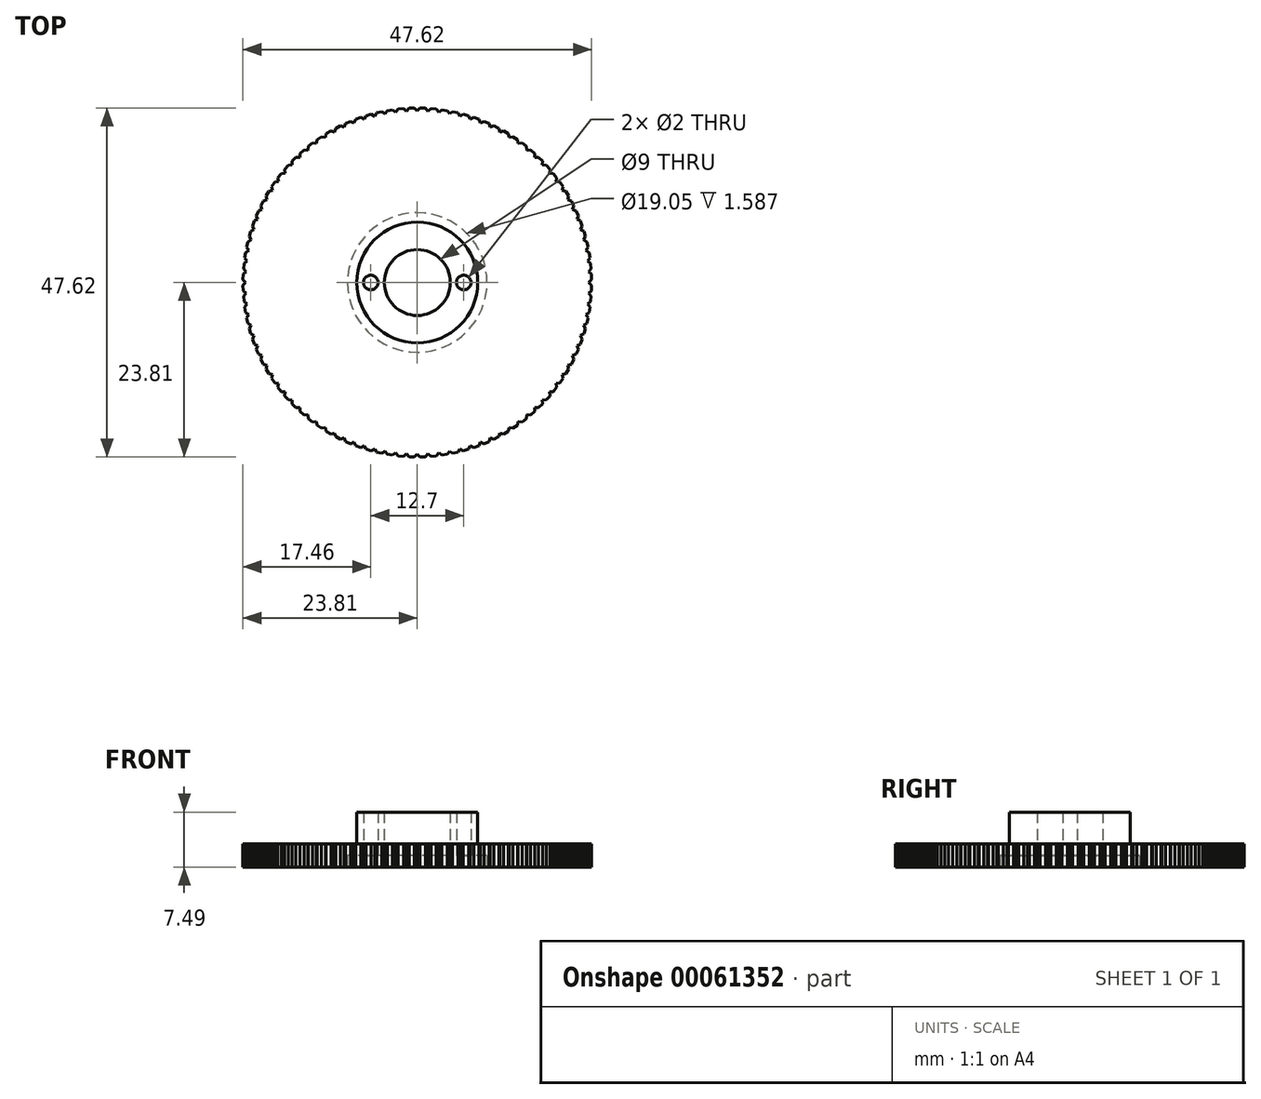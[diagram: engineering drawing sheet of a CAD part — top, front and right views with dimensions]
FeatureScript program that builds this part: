
annotation { "Feature Type Name" : "Feature", "Feature Type Description" : "" }
export const myFeature = defineFeature(function(context is Context, id is Id, definition is map)
    precondition{}
    {
        {
            var Q0;
            Q0=qCreatedBy(makeId("Top.planeOp"),FACE);
            var sketch = newSketch(context, id + "F0", { "sketchPlane" : qUnion([Q0])});
            skCircle(sketch, "E0", {"center": v(0, 0) * mm, "radius": 23.81 * mm});
            skCircle(sketch, "E1", {"center": v(0, 0) * mm, "radius": 8.26 * mm});
            skCircle(sketch, "E2", {"center": v(0, 0) * mm, "radius": 4.5 * mm});
            skSolve(sketch);
        }
        {
            var Q0;
            Q0=makeQuery(id+"F0.imprint","IMPRINT",FACE,{"disambiguationData":[TD([[makeQuery(id+"F0.imprint","IMPRINT",EDGE,{"derivedFrom":sQuery(id+"F0.wireOp",EDGE,"E0")}),1.0]])]});
            extrude(context, id + "F1", {"entities" : qUnion([Q0]), "depth" : 3.17 * mm});
        }
        {
            var Q0;
            Q0=makeQuery(id+"F0.imprint","IMPRINT",FACE,{"disambiguationData":[TD([[makeQuery(id+"F0.imprint","IMPRINT",EDGE,{"derivedFrom":sQuery(id+"F0.wireOp",EDGE,"E1")}),1.0]])]});
            extrude(context, id + "F2", {"entities" : qUnion([Q0]), "operationType" : NewBodyOperationType.ADD, "depth" : 7.5 * mm});
        }
        {
            var Q0;
            Q0=makeQuery(id+"F0.imprint","IMPRINT",FACE,{"disambiguationData":[TD([[makeQuery(id+"F0.imprint","IMPRINT",EDGE,{"derivedFrom":sQuery(id+"F0.wireOp",EDGE,"E0")}),1.0]])]});
            var sketch = newSketch(context, id + "F3", { "sketchPlane" : qUnion([Q0])});
            skCircle(sketch, "E3", {"center": v(0, 0) * mm, "radius": 9.53 * mm});
            skSolve(sketch);
        }
        {
            var Q0;
            Q0=makeQuery(id+"F3.imprint","IMPRINT",FACE,{"disambiguationData":[TD([[makeQuery(id+"F3.imprint","IMPRINT",EDGE,{"derivedFrom":sQuery(id+"F3.wireOp",EDGE,"E3")}),1.0]])]});
            var Q1;
            Q1=makeQuery(id+"F3.imprint","IMPRINT",FACE,{"disambiguationData":[TD([[makeQuery(id+"F3.imprint","IMPRINT",EDGE,{"derivedFrom":makeQuery(id+"F0.imprint","IMPRINT",EDGE,{"derivedFrom":sQuery(id+"F0.wireOp",EDGE,"E1")})}),1.0]])]});
            extrude(context, id + "F4", {"entities" : qUnion([Q0, Q1]), "operationType" : NewBodyOperationType.REMOVE, "depth" : 1.59 * mm});
        }
        {
            var Q0;
            Q0=makeQuery(id+"F4.boolean.opBoolean","COPY",FACE,{"derivedFrom":makeQuery(id+"F4.opExtrude","CAP_FACE",FACE,{"disambiguationData":[OSD([sQuery(id+"F3.wireOp",EDGE,"E3")])],"isStart":false})});
            var sketch = newSketch(context, id + "F5", { "sketchPlane" : qUnion([Q0])});
            skCircle(sketch, "E4", {"center": v(0, 0) * mm, "radius": 6.35 * mm});
            skPoint(sketch, "E5", {"position": v(-6.35, 0) * mm});
            skPoint(sketch, "E6", {"position": v(6.35, 0) * mm});
            skSolve(sketch);
        }
        {
            var Q0;
            Q0=sQuery(id+"F5.wireOp",VERTEX,"E5");
            var Q1;
            Q1=sQuery(id+"F5.wireOp",VERTEX,"E6");
            var Q2;
            Q2=makeQuery(id+"F1.opExtrude","SWEPT_BODY",BODY,{"disambiguationData":[OSD([sQuery(id+"F0.wireOp",EDGE,"E0"),sQuery(id+"F0.wireOp",EDGE,"E1")])]});
            hole(context, id + "F6", {"style" : HoleStyle.SIMPLE, "holeDiameter" : 2 * mm, "endStyle" : HoleEndStyle.THROUGH, "locations" : qUnion([Q0, Q1]), "scope" : qUnion([Q2])});
        }
        {
            var Q0;
            Q0=makeQuery(id+"F1.opExtrude","CAP_FACE",FACE,{"disambiguationData":[OSD([sQuery(id+"F0.wireOp",EDGE,"E0"),sQuery(id+"F0.wireOp",EDGE,"E1")])],"isStart":false});
            var sketch = newSketch(context, id + "F7", { "sketchPlane" : qUnion([Q0])});
            skLineSegment(sketch, "E7", {"start": v(0.37, 23.8) * mm, "end": v(0, 23.44) * mm});
            skLineSegment(sketch, "E8", {"start": v(0, 23.44) * mm, "end": v(-0.37, 23.8) * mm});
            skLineSegment(sketch, "E9.1.0", {"start": v(-1.47, 23.4) * mm, "end": v(-1.87, 23.74) * mm});
            skLineSegment(sketch, "E9.1.1", {"start": v(-1.12, 23.79) * mm, "end": v(-1.47, 23.4) * mm});
            skLineSegment(sketch, "E9.2.0", {"start": v(-2.94, 23.25) * mm, "end": v(-3.36, 23.57) * mm});
            skLineSegment(sketch, "E9.2.1", {"start": v(-2.61, 23.67) * mm, "end": v(-2.94, 23.25) * mm});
            skPoint(sketch, "E9.center", {"position": v(0, 0) * mm});
            skLineSegment(sketch, "E10.1.3.0", {"start": v(-4.4, 23.02) * mm, "end": v(-4.83, 23.32) * mm});
            skLineSegment(sketch, "E10.3.3.0", {"start": v(-4.1, 23.46) * mm, "end": v(-4.4, 23.02) * mm});
            skLineSegment(sketch, "E10.1.4.0", {"start": v(-5.83, 22.7) * mm, "end": v(-6.28, 22.97) * mm});
            skLineSegment(sketch, "E10.3.4.0", {"start": v(-5.56, 23.15) * mm, "end": v(-5.83, 22.7) * mm});
            skLineSegment(sketch, "E10.1.5.0", {"start": v(-7.24, 22.3) * mm, "end": v(-7.71, 22.53) * mm});
            skLineSegment(sketch, "E10.3.5.0", {"start": v(-7, 22.76) * mm, "end": v(-7.24, 22.3) * mm});
            skLineSegment(sketch, "E10.1.6.0", {"start": v(-8.63, 21.8) * mm, "end": v(-9.11, 22) * mm});
            skLineSegment(sketch, "E10.3.6.0", {"start": v(-8.42, 22.28) * mm, "end": v(-8.63, 21.8) * mm});
            skLineSegment(sketch, "E10.1.7.0", {"start": v(-9.98, 21.2) * mm, "end": v(-10.48, 21.38) * mm});
            skLineSegment(sketch, "E10.3.7.0", {"start": v(-9.8, 21.7) * mm, "end": v(-9.98, 21.2) * mm});
            skLineSegment(sketch, "E10.1.8.0", {"start": v(-11.3, 20.54) * mm, "end": v(-11.8, 20.68) * mm});
            skLineSegment(sketch, "E10.3.8.0", {"start": v(-11.14, 21.04) * mm, "end": v(-11.3, 20.54) * mm});
            skLineSegment(sketch, "E10.1.9.0", {"start": v(-12.56, 19.79) * mm, "end": v(-13.07, 19.9) * mm});
            skLineSegment(sketch, "E10.3.9.0", {"start": v(-12.44, 20.3) * mm, "end": v(-12.56, 19.79) * mm});
            skLineSegment(sketch, "E10.1.10.0", {"start": v(-13.78, 18.96) * mm, "end": v(-14.3, 19.04) * mm});
            skLineSegment(sketch, "E10.3.10.0", {"start": v(-13.7, 19.48) * mm, "end": v(-13.78, 18.96) * mm});
            skLineSegment(sketch, "E10.1.11.0", {"start": v(-14.94, 18.06) * mm, "end": v(-15.46, 18.1) * mm});
            skLineSegment(sketch, "E10.3.11.0", {"start": v(-14.89, 18.58) * mm, "end": v(-14.94, 18.06) * mm});
            skLineSegment(sketch, "E10.1.12.0", {"start": v(-16.04, 17.09) * mm, "end": v(-16.57, 17.1) * mm});
            skLineSegment(sketch, "E10.3.12.0", {"start": v(-16.03, 17.61) * mm, "end": v(-16.04, 17.09) * mm});
            skLineSegment(sketch, "E10.1.13.0", {"start": v(-17.09, 16.04) * mm, "end": v(-17.61, 16.03) * mm});
            skLineSegment(sketch, "E10.3.13.0", {"start": v(-17.1, 16.57) * mm, "end": v(-17.09, 16.04) * mm});
            skLineSegment(sketch, "E10.1.14.0", {"start": v(-18.06, 14.94) * mm, "end": v(-18.58, 14.89) * mm});
            skLineSegment(sketch, "E10.3.14.0", {"start": v(-18.1, 15.46) * mm, "end": v(-18.06, 14.94) * mm});
            skLineSegment(sketch, "E10.1.15.0", {"start": v(-18.96, 13.78) * mm, "end": v(-19.48, 13.7) * mm});
            skLineSegment(sketch, "E10.3.15.0", {"start": v(-19.04, 14.3) * mm, "end": v(-18.96, 13.78) * mm});
            skLineSegment(sketch, "E10.1.16.0", {"start": v(-19.79, 12.56) * mm, "end": v(-20.3, 12.44) * mm});
            skLineSegment(sketch, "E10.3.16.0", {"start": v(-19.9, 13.07) * mm, "end": v(-19.79, 12.56) * mm});
            skLineSegment(sketch, "E10.1.17.0", {"start": v(-20.54, 11.3) * mm, "end": v(-21.04, 11.14) * mm});
            skLineSegment(sketch, "E10.3.17.0", {"start": v(-20.68, 11.8) * mm, "end": v(-20.54, 11.3) * mm});
            skLineSegment(sketch, "E10.1.18.0", {"start": v(-21.2, 9.98) * mm, "end": v(-21.7, 9.8) * mm});
            skLineSegment(sketch, "E10.3.18.0", {"start": v(-21.38, 10.48) * mm, "end": v(-21.2, 9.98) * mm});
            skLineSegment(sketch, "E10.1.19.0", {"start": v(-21.8, 8.63) * mm, "end": v(-22.28, 8.42) * mm});
            skLineSegment(sketch, "E10.3.19.0", {"start": v(-22, 9.11) * mm, "end": v(-21.8, 8.63) * mm});
            skLineSegment(sketch, "E10.1.20.0", {"start": v(-22.3, 7.24) * mm, "end": v(-22.76, 7) * mm});
            skLineSegment(sketch, "E10.3.20.0", {"start": v(-22.53, 7.71) * mm, "end": v(-22.3, 7.24) * mm});
            skLineSegment(sketch, "E10.1.21.0", {"start": v(-22.7, 5.83) * mm, "end": v(-23.15, 5.56) * mm});
            skLineSegment(sketch, "E10.3.21.0", {"start": v(-22.97, 6.28) * mm, "end": v(-22.7, 5.83) * mm});
            skLineSegment(sketch, "E10.1.22.0", {"start": v(-23.02, 4.4) * mm, "end": v(-23.46, 4.1) * mm});
            skLineSegment(sketch, "E10.3.22.0", {"start": v(-23.32, 4.83) * mm, "end": v(-23.02, 4.4) * mm});
            skLineSegment(sketch, "E10.1.23.0", {"start": v(-23.25, 2.94) * mm, "end": v(-23.67, 2.61) * mm});
            skLineSegment(sketch, "E10.3.23.0", {"start": v(-23.57, 3.36) * mm, "end": v(-23.25, 2.94) * mm});
            skLineSegment(sketch, "E10.1.24.0", {"start": v(-23.4, 1.47) * mm, "end": v(-23.79, 1.12) * mm});
            skLineSegment(sketch, "E10.3.24.0", {"start": v(-23.74, 1.87) * mm, "end": v(-23.4, 1.47) * mm});
            skLineSegment(sketch, "E10.1.25.0", {"start": v(-23.44, 0) * mm, "end": v(-23.8, -0.37) * mm});
            skLineSegment(sketch, "E10.3.25.0", {"start": v(-23.8, 0.37) * mm, "end": v(-23.44, 0) * mm});
            skLineSegment(sketch, "E10.1.26.0", {"start": v(-23.4, -1.47) * mm, "end": v(-23.74, -1.87) * mm});
            skLineSegment(sketch, "E10.3.26.0", {"start": v(-23.79, -1.12) * mm, "end": v(-23.4, -1.47) * mm});
            skLineSegment(sketch, "E10.1.27.0", {"start": v(-23.25, -2.94) * mm, "end": v(-23.57, -3.36) * mm});
            skLineSegment(sketch, "E10.3.27.0", {"start": v(-23.67, -2.61) * mm, "end": v(-23.25, -2.94) * mm});
            skLineSegment(sketch, "E10.1.28.0", {"start": v(-23.02, -4.4) * mm, "end": v(-23.32, -4.83) * mm});
            skLineSegment(sketch, "E10.3.28.0", {"start": v(-23.46, -4.1) * mm, "end": v(-23.02, -4.4) * mm});
            skLineSegment(sketch, "E10.1.29.0", {"start": v(-22.7, -5.83) * mm, "end": v(-22.97, -6.28) * mm});
            skLineSegment(sketch, "E10.3.29.0", {"start": v(-23.15, -5.56) * mm, "end": v(-22.7, -5.83) * mm});
            skLineSegment(sketch, "E10.1.30.0", {"start": v(-22.3, -7.24) * mm, "end": v(-22.53, -7.71) * mm});
            skLineSegment(sketch, "E10.3.30.0", {"start": v(-22.76, -7) * mm, "end": v(-22.3, -7.24) * mm});
            skLineSegment(sketch, "E10.1.31.0", {"start": v(-21.8, -8.63) * mm, "end": v(-22, -9.11) * mm});
            skLineSegment(sketch, "E10.3.31.0", {"start": v(-22.28, -8.42) * mm, "end": v(-21.8, -8.63) * mm});
            skLineSegment(sketch, "E10.1.32.0", {"start": v(-21.2, -9.98) * mm, "end": v(-21.38, -10.48) * mm});
            skLineSegment(sketch, "E10.3.32.0", {"start": v(-21.7, -9.8) * mm, "end": v(-21.2, -9.98) * mm});
            skLineSegment(sketch, "E10.1.33.0", {"start": v(-20.54, -11.3) * mm, "end": v(-20.68, -11.8) * mm});
            skLineSegment(sketch, "E10.3.33.0", {"start": v(-21.04, -11.14) * mm, "end": v(-20.54, -11.3) * mm});
            skLineSegment(sketch, "E10.1.34.0", {"start": v(-19.79, -12.56) * mm, "end": v(-19.9, -13.07) * mm});
            skLineSegment(sketch, "E10.3.34.0", {"start": v(-20.3, -12.44) * mm, "end": v(-19.79, -12.56) * mm});
            skLineSegment(sketch, "E10.1.35.0", {"start": v(-18.96, -13.78) * mm, "end": v(-19.04, -14.3) * mm});
            skLineSegment(sketch, "E10.3.35.0", {"start": v(-19.48, -13.7) * mm, "end": v(-18.96, -13.78) * mm});
            skLineSegment(sketch, "E10.1.36.0", {"start": v(-18.06, -14.94) * mm, "end": v(-18.1, -15.46) * mm});
            skLineSegment(sketch, "E10.3.36.0", {"start": v(-18.58, -14.89) * mm, "end": v(-18.06, -14.94) * mm});
            skLineSegment(sketch, "E10.1.37.0", {"start": v(-17.09, -16.04) * mm, "end": v(-17.1, -16.57) * mm});
            skLineSegment(sketch, "E10.3.37.0", {"start": v(-17.61, -16.03) * mm, "end": v(-17.09, -16.04) * mm});
            skLineSegment(sketch, "E10.1.38.0", {"start": v(-16.04, -17.09) * mm, "end": v(-16.03, -17.61) * mm});
            skLineSegment(sketch, "E10.3.38.0", {"start": v(-16.57, -17.1) * mm, "end": v(-16.04, -17.09) * mm});
            skLineSegment(sketch, "E10.1.39.0", {"start": v(-14.94, -18.06) * mm, "end": v(-14.89, -18.58) * mm});
            skLineSegment(sketch, "E10.3.39.0", {"start": v(-15.46, -18.1) * mm, "end": v(-14.94, -18.06) * mm});
            skLineSegment(sketch, "E10.1.40.0", {"start": v(-13.78, -18.96) * mm, "end": v(-13.7, -19.48) * mm});
            skLineSegment(sketch, "E10.3.40.0", {"start": v(-14.3, -19.04) * mm, "end": v(-13.78, -18.96) * mm});
            skLineSegment(sketch, "E10.1.41.0", {"start": v(-12.56, -19.79) * mm, "end": v(-12.44, -20.3) * mm});
            skLineSegment(sketch, "E10.3.41.0", {"start": v(-13.07, -19.9) * mm, "end": v(-12.56, -19.79) * mm});
            skLineSegment(sketch, "E10.1.42.0", {"start": v(-11.3, -20.54) * mm, "end": v(-11.14, -21.04) * mm});
            skLineSegment(sketch, "E10.3.42.0", {"start": v(-11.8, -20.68) * mm, "end": v(-11.3, -20.54) * mm});
            skLineSegment(sketch, "E10.1.43.0", {"start": v(-9.98, -21.2) * mm, "end": v(-9.8, -21.7) * mm});
            skLineSegment(sketch, "E10.3.43.0", {"start": v(-10.48, -21.38) * mm, "end": v(-9.98, -21.2) * mm});
            skLineSegment(sketch, "E10.1.44.0", {"start": v(-8.63, -21.8) * mm, "end": v(-8.42, -22.28) * mm});
            skLineSegment(sketch, "E10.3.44.0", {"start": v(-9.11, -22) * mm, "end": v(-8.63, -21.8) * mm});
            skLineSegment(sketch, "E10.1.45.0", {"start": v(-7.24, -22.3) * mm, "end": v(-7, -22.76) * mm});
            skLineSegment(sketch, "E10.3.45.0", {"start": v(-7.71, -22.53) * mm, "end": v(-7.24, -22.3) * mm});
            skLineSegment(sketch, "E10.1.46.0", {"start": v(-5.83, -22.7) * mm, "end": v(-5.56, -23.15) * mm});
            skLineSegment(sketch, "E10.3.46.0", {"start": v(-6.28, -22.97) * mm, "end": v(-5.83, -22.7) * mm});
            skLineSegment(sketch, "E10.1.47.0", {"start": v(-4.4, -23.02) * mm, "end": v(-4.1, -23.46) * mm});
            skLineSegment(sketch, "E10.3.47.0", {"start": v(-4.83, -23.32) * mm, "end": v(-4.4, -23.02) * mm});
            skLineSegment(sketch, "E10.1.48.0", {"start": v(-2.94, -23.25) * mm, "end": v(-2.61, -23.67) * mm});
            skLineSegment(sketch, "E10.3.48.0", {"start": v(-3.36, -23.57) * mm, "end": v(-2.94, -23.25) * mm});
            skLineSegment(sketch, "E10.1.49.0", {"start": v(-1.47, -23.4) * mm, "end": v(-1.12, -23.79) * mm});
            skLineSegment(sketch, "E10.3.49.0", {"start": v(-1.87, -23.74) * mm, "end": v(-1.47, -23.4) * mm});
            skLineSegment(sketch, "E10.1.50.0", {"start": v(0, -23.44) * mm, "end": v(0.37, -23.8) * mm});
            skLineSegment(sketch, "E10.3.50.0", {"start": v(-0.37, -23.8) * mm, "end": v(0, -23.44) * mm});
            skLineSegment(sketch, "E10.1.51.0", {"start": v(1.47, -23.4) * mm, "end": v(1.87, -23.74) * mm});
            skLineSegment(sketch, "E10.3.51.0", {"start": v(1.12, -23.79) * mm, "end": v(1.47, -23.4) * mm});
            skLineSegment(sketch, "E10.1.52.0", {"start": v(2.94, -23.25) * mm, "end": v(3.36, -23.57) * mm});
            skLineSegment(sketch, "E10.3.52.0", {"start": v(2.61, -23.67) * mm, "end": v(2.94, -23.25) * mm});
            skLineSegment(sketch, "E10.1.53.0", {"start": v(4.4, -23.02) * mm, "end": v(4.83, -23.32) * mm});
            skLineSegment(sketch, "E10.3.53.0", {"start": v(4.1, -23.46) * mm, "end": v(4.4, -23.02) * mm});
            skLineSegment(sketch, "E10.1.54.0", {"start": v(5.83, -22.7) * mm, "end": v(6.28, -22.97) * mm});
            skLineSegment(sketch, "E10.3.54.0", {"start": v(5.56, -23.15) * mm, "end": v(5.83, -22.7) * mm});
            skLineSegment(sketch, "E10.1.55.0", {"start": v(7.24, -22.3) * mm, "end": v(7.71, -22.53) * mm});
            skLineSegment(sketch, "E10.3.55.0", {"start": v(7, -22.76) * mm, "end": v(7.24, -22.3) * mm});
            skLineSegment(sketch, "E10.1.56.0", {"start": v(8.63, -21.8) * mm, "end": v(9.11, -22) * mm});
            skLineSegment(sketch, "E10.3.56.0", {"start": v(8.42, -22.28) * mm, "end": v(8.63, -21.8) * mm});
            skLineSegment(sketch, "E10.1.57.0", {"start": v(9.98, -21.2) * mm, "end": v(10.48, -21.38) * mm});
            skLineSegment(sketch, "E10.3.57.0", {"start": v(9.8, -21.7) * mm, "end": v(9.98, -21.2) * mm});
            skLineSegment(sketch, "E10.1.58.0", {"start": v(11.3, -20.54) * mm, "end": v(11.8, -20.68) * mm});
            skLineSegment(sketch, "E10.3.58.0", {"start": v(11.14, -21.04) * mm, "end": v(11.3, -20.54) * mm});
            skLineSegment(sketch, "E10.1.59.0", {"start": v(12.56, -19.79) * mm, "end": v(13.07, -19.9) * mm});
            skLineSegment(sketch, "E10.3.59.0", {"start": v(12.44, -20.3) * mm, "end": v(12.56, -19.79) * mm});
            skLineSegment(sketch, "E10.1.60.0", {"start": v(13.78, -18.96) * mm, "end": v(14.3, -19.04) * mm});
            skLineSegment(sketch, "E10.3.60.0", {"start": v(13.7, -19.48) * mm, "end": v(13.78, -18.96) * mm});
            skLineSegment(sketch, "E10.1.61.0", {"start": v(14.94, -18.06) * mm, "end": v(15.46, -18.1) * mm});
            skLineSegment(sketch, "E10.3.61.0", {"start": v(14.89, -18.58) * mm, "end": v(14.94, -18.06) * mm});
            skLineSegment(sketch, "E10.1.62.0", {"start": v(16.04, -17.09) * mm, "end": v(16.57, -17.1) * mm});
            skLineSegment(sketch, "E10.3.62.0", {"start": v(16.03, -17.61) * mm, "end": v(16.04, -17.09) * mm});
            skLineSegment(sketch, "E10.1.63.0", {"start": v(17.09, -16.04) * mm, "end": v(17.61, -16.03) * mm});
            skLineSegment(sketch, "E10.3.63.0", {"start": v(17.1, -16.57) * mm, "end": v(17.09, -16.04) * mm});
            skLineSegment(sketch, "E10.1.64.0", {"start": v(18.06, -14.94) * mm, "end": v(18.58, -14.89) * mm});
            skLineSegment(sketch, "E10.3.64.0", {"start": v(18.1, -15.46) * mm, "end": v(18.06, -14.94) * mm});
            skLineSegment(sketch, "E10.1.65.0", {"start": v(18.96, -13.78) * mm, "end": v(19.48, -13.7) * mm});
            skLineSegment(sketch, "E10.3.65.0", {"start": v(19.04, -14.3) * mm, "end": v(18.96, -13.78) * mm});
            skLineSegment(sketch, "E10.1.66.0", {"start": v(19.79, -12.56) * mm, "end": v(20.3, -12.44) * mm});
            skLineSegment(sketch, "E10.3.66.0", {"start": v(19.9, -13.07) * mm, "end": v(19.79, -12.56) * mm});
            skLineSegment(sketch, "E10.1.67.0", {"start": v(20.54, -11.3) * mm, "end": v(21.04, -11.14) * mm});
            skLineSegment(sketch, "E10.3.67.0", {"start": v(20.68, -11.8) * mm, "end": v(20.54, -11.3) * mm});
            skLineSegment(sketch, "E10.1.68.0", {"start": v(21.2, -9.98) * mm, "end": v(21.7, -9.8) * mm});
            skLineSegment(sketch, "E10.3.68.0", {"start": v(21.38, -10.48) * mm, "end": v(21.2, -9.98) * mm});
            skLineSegment(sketch, "E10.1.69.0", {"start": v(21.8, -8.63) * mm, "end": v(22.28, -8.42) * mm});
            skLineSegment(sketch, "E10.3.69.0", {"start": v(22, -9.11) * mm, "end": v(21.8, -8.63) * mm});
            skLineSegment(sketch, "E10.1.70.0", {"start": v(22.3, -7.24) * mm, "end": v(22.76, -7) * mm});
            skLineSegment(sketch, "E10.3.70.0", {"start": v(22.53, -7.71) * mm, "end": v(22.3, -7.24) * mm});
            skLineSegment(sketch, "E10.1.71.0", {"start": v(22.7, -5.83) * mm, "end": v(23.15, -5.56) * mm});
            skLineSegment(sketch, "E10.3.71.0", {"start": v(22.97, -6.28) * mm, "end": v(22.7, -5.83) * mm});
            skLineSegment(sketch, "E10.1.72.0", {"start": v(23.02, -4.4) * mm, "end": v(23.46, -4.1) * mm});
            skLineSegment(sketch, "E10.3.72.0", {"start": v(23.32, -4.83) * mm, "end": v(23.02, -4.4) * mm});
            skLineSegment(sketch, "E10.1.73.0", {"start": v(23.25, -2.94) * mm, "end": v(23.67, -2.61) * mm});
            skLineSegment(sketch, "E10.3.73.0", {"start": v(23.57, -3.36) * mm, "end": v(23.25, -2.94) * mm});
            skLineSegment(sketch, "E10.1.74.0", {"start": v(23.4, -1.47) * mm, "end": v(23.79, -1.12) * mm});
            skLineSegment(sketch, "E10.3.74.0", {"start": v(23.74, -1.87) * mm, "end": v(23.4, -1.47) * mm});
            skLineSegment(sketch, "E10.1.75.0", {"start": v(23.44, 0) * mm, "end": v(23.8, 0.37) * mm});
            skLineSegment(sketch, "E10.3.75.0", {"start": v(23.8, -0.37) * mm, "end": v(23.44, 0) * mm});
            skLineSegment(sketch, "E10.1.76.0", {"start": v(23.4, 1.47) * mm, "end": v(23.74, 1.87) * mm});
            skLineSegment(sketch, "E10.3.76.0", {"start": v(23.79, 1.12) * mm, "end": v(23.4, 1.47) * mm});
            skLineSegment(sketch, "E10.1.77.0", {"start": v(23.25, 2.94) * mm, "end": v(23.57, 3.36) * mm});
            skLineSegment(sketch, "E10.3.77.0", {"start": v(23.67, 2.61) * mm, "end": v(23.25, 2.94) * mm});
            skLineSegment(sketch, "E10.1.78.0", {"start": v(23.02, 4.4) * mm, "end": v(23.32, 4.83) * mm});
            skLineSegment(sketch, "E10.3.78.0", {"start": v(23.46, 4.1) * mm, "end": v(23.02, 4.4) * mm});
            skLineSegment(sketch, "E10.1.79.0", {"start": v(22.7, 5.83) * mm, "end": v(22.97, 6.28) * mm});
            skLineSegment(sketch, "E10.3.79.0", {"start": v(23.15, 5.56) * mm, "end": v(22.7, 5.83) * mm});
            skLineSegment(sketch, "E10.1.80.0", {"start": v(22.3, 7.24) * mm, "end": v(22.53, 7.71) * mm});
            skLineSegment(sketch, "E10.3.80.0", {"start": v(22.76, 7) * mm, "end": v(22.3, 7.24) * mm});
            skLineSegment(sketch, "E10.1.81.0", {"start": v(21.8, 8.63) * mm, "end": v(22, 9.11) * mm});
            skLineSegment(sketch, "E10.3.81.0", {"start": v(22.28, 8.42) * mm, "end": v(21.8, 8.63) * mm});
            skLineSegment(sketch, "E10.1.82.0", {"start": v(21.2, 9.98) * mm, "end": v(21.38, 10.48) * mm});
            skLineSegment(sketch, "E10.3.82.0", {"start": v(21.7, 9.8) * mm, "end": v(21.2, 9.98) * mm});
            skLineSegment(sketch, "E10.1.83.0", {"start": v(20.54, 11.3) * mm, "end": v(20.68, 11.8) * mm});
            skLineSegment(sketch, "E10.3.83.0", {"start": v(21.04, 11.14) * mm, "end": v(20.54, 11.3) * mm});
            skLineSegment(sketch, "E10.1.84.0", {"start": v(19.79, 12.56) * mm, "end": v(19.9, 13.07) * mm});
            skLineSegment(sketch, "E10.3.84.0", {"start": v(20.3, 12.44) * mm, "end": v(19.79, 12.56) * mm});
            skLineSegment(sketch, "E10.1.85.0", {"start": v(18.96, 13.78) * mm, "end": v(19.04, 14.3) * mm});
            skLineSegment(sketch, "E10.3.85.0", {"start": v(19.48, 13.7) * mm, "end": v(18.96, 13.78) * mm});
            skLineSegment(sketch, "E10.1.86.0", {"start": v(18.06, 14.94) * mm, "end": v(18.1, 15.46) * mm});
            skLineSegment(sketch, "E10.3.86.0", {"start": v(18.58, 14.89) * mm, "end": v(18.06, 14.94) * mm});
            skLineSegment(sketch, "E10.1.87.0", {"start": v(17.09, 16.04) * mm, "end": v(17.1, 16.57) * mm});
            skLineSegment(sketch, "E10.3.87.0", {"start": v(17.61, 16.03) * mm, "end": v(17.09, 16.04) * mm});
            skLineSegment(sketch, "E10.1.88.0", {"start": v(16.04, 17.09) * mm, "end": v(16.03, 17.61) * mm});
            skLineSegment(sketch, "E10.3.88.0", {"start": v(16.57, 17.1) * mm, "end": v(16.04, 17.09) * mm});
            skLineSegment(sketch, "E10.1.89.0", {"start": v(14.94, 18.06) * mm, "end": v(14.89, 18.58) * mm});
            skLineSegment(sketch, "E10.3.89.0", {"start": v(15.46, 18.1) * mm, "end": v(14.94, 18.06) * mm});
            skLineSegment(sketch, "E10.1.90.0", {"start": v(13.78, 18.96) * mm, "end": v(13.7, 19.48) * mm});
            skLineSegment(sketch, "E10.3.90.0", {"start": v(14.3, 19.04) * mm, "end": v(13.78, 18.96) * mm});
            skLineSegment(sketch, "E10.1.91.0", {"start": v(12.56, 19.79) * mm, "end": v(12.44, 20.3) * mm});
            skLineSegment(sketch, "E10.3.91.0", {"start": v(13.07, 19.9) * mm, "end": v(12.56, 19.79) * mm});
            skLineSegment(sketch, "E10.1.92.0", {"start": v(11.3, 20.54) * mm, "end": v(11.14, 21.04) * mm});
            skLineSegment(sketch, "E10.3.92.0", {"start": v(11.8, 20.68) * mm, "end": v(11.3, 20.54) * mm});
            skLineSegment(sketch, "E10.1.93.0", {"start": v(9.98, 21.2) * mm, "end": v(9.8, 21.7) * mm});
            skLineSegment(sketch, "E10.3.93.0", {"start": v(10.48, 21.38) * mm, "end": v(9.98, 21.2) * mm});
            skLineSegment(sketch, "E10.1.94.0", {"start": v(8.63, 21.8) * mm, "end": v(8.42, 22.28) * mm});
            skLineSegment(sketch, "E10.3.94.0", {"start": v(9.11, 22) * mm, "end": v(8.63, 21.8) * mm});
            skLineSegment(sketch, "E10.1.95.0", {"start": v(7.24, 22.3) * mm, "end": v(7, 22.76) * mm});
            skLineSegment(sketch, "E10.3.95.0", {"start": v(7.71, 22.53) * mm, "end": v(7.24, 22.3) * mm});
            skLineSegment(sketch, "E10.1.96.0", {"start": v(5.83, 22.7) * mm, "end": v(5.56, 23.15) * mm});
            skLineSegment(sketch, "E10.3.96.0", {"start": v(6.28, 22.97) * mm, "end": v(5.83, 22.7) * mm});
            skLineSegment(sketch, "E10.1.97.0", {"start": v(4.4, 23.02) * mm, "end": v(4.1, 23.46) * mm});
            skLineSegment(sketch, "E10.3.97.0", {"start": v(4.83, 23.32) * mm, "end": v(4.4, 23.02) * mm});
            skLineSegment(sketch, "E10.1.98.0", {"start": v(2.94, 23.25) * mm, "end": v(2.61, 23.67) * mm});
            skLineSegment(sketch, "E10.3.98.0", {"start": v(3.36, 23.57) * mm, "end": v(2.94, 23.25) * mm});
            skLineSegment(sketch, "E10.1.99.0", {"start": v(1.47, 23.4) * mm, "end": v(1.12, 23.79) * mm});
            skLineSegment(sketch, "E10.3.99.0", {"start": v(1.87, 23.74) * mm, "end": v(1.47, 23.4) * mm});
            skLineSegment(sketch, "E11", {"start": v(-1.12, 23.79) * mm, "end": v(-0.37, 23.8) * mm});
            skLineSegment(sketch, "E12.1.0", {"start": v(-2.61, 23.67) * mm, "end": v(-1.87, 23.74) * mm});
            skLineSegment(sketch, "E12.2.0", {"start": v(-4.1, 23.46) * mm, "end": v(-3.36, 23.57) * mm});
            skLineSegment(sketch, "E12.3.0", {"start": v(-5.56, 23.15) * mm, "end": v(-4.83, 23.32) * mm});
            skLineSegment(sketch, "E12.4.0", {"start": v(-7, 22.76) * mm, "end": v(-6.28, 22.97) * mm});
            skLineSegment(sketch, "E12.5.0", {"start": v(-8.42, 22.28) * mm, "end": v(-7.71, 22.53) * mm});
            skLineSegment(sketch, "E12.6.0", {"start": v(-9.8, 21.7) * mm, "end": v(-9.11, 22) * mm});
            skLineSegment(sketch, "E12.7.0", {"start": v(-11.14, 21.04) * mm, "end": v(-10.48, 21.38) * mm});
            skLineSegment(sketch, "E12.8.0", {"start": v(-12.44, 20.3) * mm, "end": v(-11.8, 20.68) * mm});
            skLineSegment(sketch, "E12.9.0", {"start": v(-13.7, 19.48) * mm, "end": v(-13.07, 19.9) * mm});
            skLineSegment(sketch, "E12.10.0", {"start": v(-14.89, 18.58) * mm, "end": v(-14.3, 19.04) * mm});
            skLineSegment(sketch, "E12.11.0", {"start": v(-16.03, 17.61) * mm, "end": v(-15.46, 18.1) * mm});
            skLineSegment(sketch, "E12.12.0", {"start": v(-17.1, 16.57) * mm, "end": v(-16.57, 17.1) * mm});
            skLineSegment(sketch, "E12.13.0", {"start": v(-18.1, 15.46) * mm, "end": v(-17.61, 16.03) * mm});
            skLineSegment(sketch, "E12.14.0", {"start": v(-19.04, 14.3) * mm, "end": v(-18.58, 14.89) * mm});
            skLineSegment(sketch, "E12.15.0", {"start": v(-19.9, 13.07) * mm, "end": v(-19.48, 13.7) * mm});
            skLineSegment(sketch, "E12.16.0", {"start": v(-20.68, 11.8) * mm, "end": v(-20.3, 12.44) * mm});
            skLineSegment(sketch, "E12.17.0", {"start": v(-21.38, 10.48) * mm, "end": v(-21.04, 11.14) * mm});
            skLineSegment(sketch, "E12.18.0", {"start": v(-22, 9.11) * mm, "end": v(-21.7, 9.8) * mm});
            skLineSegment(sketch, "E12.19.0", {"start": v(-22.53, 7.71) * mm, "end": v(-22.28, 8.42) * mm});
            skLineSegment(sketch, "E12.20.0", {"start": v(-22.97, 6.28) * mm, "end": v(-22.76, 7) * mm});
            skLineSegment(sketch, "E12.21.0", {"start": v(-23.32, 4.83) * mm, "end": v(-23.15, 5.56) * mm});
            skLineSegment(sketch, "E12.22.0", {"start": v(-23.57, 3.36) * mm, "end": v(-23.46, 4.1) * mm});
            skLineSegment(sketch, "E12.23.0", {"start": v(-23.74, 1.87) * mm, "end": v(-23.67, 2.61) * mm});
            skLineSegment(sketch, "E12.24.0", {"start": v(-23.8, 0.37) * mm, "end": v(-23.79, 1.12) * mm});
            skLineSegment(sketch, "E12.25.0", {"start": v(-23.79, -1.12) * mm, "end": v(-23.8, -0.37) * mm});
            skLineSegment(sketch, "E12.26.0", {"start": v(-23.67, -2.61) * mm, "end": v(-23.74, -1.87) * mm});
            skLineSegment(sketch, "E12.27.0", {"start": v(-23.46, -4.1) * mm, "end": v(-23.57, -3.36) * mm});
            skLineSegment(sketch, "E12.28.0", {"start": v(-23.15, -5.56) * mm, "end": v(-23.32, -4.83) * mm});
            skLineSegment(sketch, "E12.29.0", {"start": v(-22.76, -7) * mm, "end": v(-22.97, -6.28) * mm});
            skLineSegment(sketch, "E12.30.0", {"start": v(-22.28, -8.42) * mm, "end": v(-22.53, -7.71) * mm});
            skLineSegment(sketch, "E12.31.0", {"start": v(-21.7, -9.8) * mm, "end": v(-22, -9.11) * mm});
            skLineSegment(sketch, "E12.32.0", {"start": v(-21.04, -11.14) * mm, "end": v(-21.38, -10.48) * mm});
            skLineSegment(sketch, "E12.33.0", {"start": v(-20.3, -12.44) * mm, "end": v(-20.68, -11.8) * mm});
            skLineSegment(sketch, "E12.34.0", {"start": v(-19.48, -13.7) * mm, "end": v(-19.9, -13.07) * mm});
            skLineSegment(sketch, "E12.35.0", {"start": v(-18.58, -14.89) * mm, "end": v(-19.04, -14.3) * mm});
            skLineSegment(sketch, "E12.36.0", {"start": v(-17.61, -16.03) * mm, "end": v(-18.1, -15.46) * mm});
            skLineSegment(sketch, "E12.37.0", {"start": v(-16.57, -17.1) * mm, "end": v(-17.1, -16.57) * mm});
            skLineSegment(sketch, "E12.38.0", {"start": v(-15.46, -18.1) * mm, "end": v(-16.03, -17.61) * mm});
            skLineSegment(sketch, "E12.39.0", {"start": v(-14.3, -19.04) * mm, "end": v(-14.89, -18.58) * mm});
            skLineSegment(sketch, "E12.40.0", {"start": v(-13.07, -19.9) * mm, "end": v(-13.7, -19.48) * mm});
            skLineSegment(sketch, "E12.41.0", {"start": v(-11.8, -20.68) * mm, "end": v(-12.44, -20.3) * mm});
            skLineSegment(sketch, "E12.42.0", {"start": v(-10.48, -21.38) * mm, "end": v(-11.14, -21.04) * mm});
            skLineSegment(sketch, "E12.43.0", {"start": v(-9.11, -22) * mm, "end": v(-9.8, -21.7) * mm});
            skLineSegment(sketch, "E12.44.0", {"start": v(-7.71, -22.53) * mm, "end": v(-8.42, -22.28) * mm});
            skLineSegment(sketch, "E12.45.0", {"start": v(-6.28, -22.97) * mm, "end": v(-7, -22.76) * mm});
            skLineSegment(sketch, "E12.46.0", {"start": v(-4.83, -23.32) * mm, "end": v(-5.56, -23.15) * mm});
            skLineSegment(sketch, "E12.47.0", {"start": v(-3.36, -23.57) * mm, "end": v(-4.1, -23.46) * mm});
            skLineSegment(sketch, "E12.48.0", {"start": v(-1.87, -23.74) * mm, "end": v(-2.61, -23.67) * mm});
            skLineSegment(sketch, "E12.49.0", {"start": v(-0.37, -23.8) * mm, "end": v(-1.12, -23.79) * mm});
            skLineSegment(sketch, "E12.50.0", {"start": v(1.12, -23.79) * mm, "end": v(0.37, -23.8) * mm});
            skLineSegment(sketch, "E12.51.0", {"start": v(2.61, -23.67) * mm, "end": v(1.87, -23.74) * mm});
            skLineSegment(sketch, "E12.52.0", {"start": v(4.1, -23.46) * mm, "end": v(3.36, -23.57) * mm});
            skLineSegment(sketch, "E12.53.0", {"start": v(5.56, -23.15) * mm, "end": v(4.83, -23.32) * mm});
            skLineSegment(sketch, "E12.54.0", {"start": v(7, -22.76) * mm, "end": v(6.28, -22.97) * mm});
            skLineSegment(sketch, "E12.55.0", {"start": v(8.42, -22.28) * mm, "end": v(7.71, -22.53) * mm});
            skLineSegment(sketch, "E12.56.0", {"start": v(9.8, -21.7) * mm, "end": v(9.11, -22) * mm});
            skLineSegment(sketch, "E12.57.0", {"start": v(11.14, -21.04) * mm, "end": v(10.48, -21.38) * mm});
            skLineSegment(sketch, "E12.58.0", {"start": v(12.44, -20.3) * mm, "end": v(11.8, -20.68) * mm});
            skLineSegment(sketch, "E12.59.0", {"start": v(13.7, -19.48) * mm, "end": v(13.07, -19.9) * mm});
            skLineSegment(sketch, "E12.60.0", {"start": v(14.89, -18.58) * mm, "end": v(14.3, -19.04) * mm});
            skLineSegment(sketch, "E12.61.0", {"start": v(16.03, -17.61) * mm, "end": v(15.46, -18.1) * mm});
            skLineSegment(sketch, "E12.62.0", {"start": v(17.1, -16.57) * mm, "end": v(16.57, -17.1) * mm});
            skLineSegment(sketch, "E12.63.0", {"start": v(18.1, -15.46) * mm, "end": v(17.61, -16.03) * mm});
            skLineSegment(sketch, "E12.64.0", {"start": v(19.04, -14.3) * mm, "end": v(18.58, -14.89) * mm});
            skLineSegment(sketch, "E12.65.0", {"start": v(19.9, -13.07) * mm, "end": v(19.48, -13.7) * mm});
            skLineSegment(sketch, "E12.66.0", {"start": v(20.68, -11.8) * mm, "end": v(20.3, -12.44) * mm});
            skLineSegment(sketch, "E12.67.0", {"start": v(21.38, -10.48) * mm, "end": v(21.04, -11.14) * mm});
            skLineSegment(sketch, "E12.68.0", {"start": v(22, -9.11) * mm, "end": v(21.7, -9.8) * mm});
            skLineSegment(sketch, "E12.69.0", {"start": v(22.53, -7.71) * mm, "end": v(22.28, -8.42) * mm});
            skLineSegment(sketch, "E12.70.0", {"start": v(22.97, -6.28) * mm, "end": v(22.76, -7) * mm});
            skLineSegment(sketch, "E12.71.0", {"start": v(23.32, -4.83) * mm, "end": v(23.15, -5.56) * mm});
            skLineSegment(sketch, "E12.72.0", {"start": v(23.57, -3.36) * mm, "end": v(23.46, -4.1) * mm});
            skLineSegment(sketch, "E12.73.0", {"start": v(23.74, -1.87) * mm, "end": v(23.67, -2.61) * mm});
            skLineSegment(sketch, "E12.74.0", {"start": v(23.8, -0.37) * mm, "end": v(23.79, -1.12) * mm});
            skLineSegment(sketch, "E12.75.0", {"start": v(23.79, 1.12) * mm, "end": v(23.8, 0.37) * mm});
            skLineSegment(sketch, "E12.76.0", {"start": v(23.67, 2.61) * mm, "end": v(23.74, 1.87) * mm});
            skLineSegment(sketch, "E12.77.0", {"start": v(23.46, 4.1) * mm, "end": v(23.57, 3.36) * mm});
            skLineSegment(sketch, "E12.78.0", {"start": v(23.15, 5.56) * mm, "end": v(23.32, 4.83) * mm});
            skLineSegment(sketch, "E12.79.0", {"start": v(22.76, 7) * mm, "end": v(22.97, 6.28) * mm});
            skLineSegment(sketch, "E12.80.0", {"start": v(22.28, 8.42) * mm, "end": v(22.53, 7.71) * mm});
            skLineSegment(sketch, "E12.81.0", {"start": v(21.7, 9.8) * mm, "end": v(22, 9.11) * mm});
            skLineSegment(sketch, "E12.82.0", {"start": v(21.04, 11.14) * mm, "end": v(21.38, 10.48) * mm});
            skLineSegment(sketch, "E12.83.0", {"start": v(20.3, 12.44) * mm, "end": v(20.68, 11.8) * mm});
            skLineSegment(sketch, "E12.84.0", {"start": v(19.48, 13.7) * mm, "end": v(19.9, 13.07) * mm});
            skLineSegment(sketch, "E12.85.0", {"start": v(18.58, 14.89) * mm, "end": v(19.04, 14.3) * mm});
            skLineSegment(sketch, "E12.86.0", {"start": v(17.61, 16.03) * mm, "end": v(18.1, 15.46) * mm});
            skLineSegment(sketch, "E12.87.0", {"start": v(16.57, 17.1) * mm, "end": v(17.1, 16.57) * mm});
            skLineSegment(sketch, "E12.88.0", {"start": v(15.46, 18.1) * mm, "end": v(16.03, 17.61) * mm});
            skLineSegment(sketch, "E12.89.0", {"start": v(14.3, 19.04) * mm, "end": v(14.89, 18.58) * mm});
            skLineSegment(sketch, "E12.90.0", {"start": v(13.07, 19.9) * mm, "end": v(13.7, 19.48) * mm});
            skLineSegment(sketch, "E12.91.0", {"start": v(11.8, 20.68) * mm, "end": v(12.44, 20.3) * mm});
            skLineSegment(sketch, "E12.92.0", {"start": v(10.48, 21.38) * mm, "end": v(11.14, 21.04) * mm});
            skLineSegment(sketch, "E12.93.0", {"start": v(9.11, 22) * mm, "end": v(9.8, 21.7) * mm});
            skLineSegment(sketch, "E12.94.0", {"start": v(7.71, 22.53) * mm, "end": v(8.42, 22.28) * mm});
            skLineSegment(sketch, "E12.95.0", {"start": v(6.28, 22.97) * mm, "end": v(7, 22.76) * mm});
            skLineSegment(sketch, "E12.96.0", {"start": v(4.83, 23.32) * mm, "end": v(5.56, 23.15) * mm});
            skLineSegment(sketch, "E12.97.0", {"start": v(3.36, 23.57) * mm, "end": v(4.1, 23.46) * mm});
            skLineSegment(sketch, "E12.98.0", {"start": v(1.87, 23.74) * mm, "end": v(2.61, 23.67) * mm});
            skLineSegment(sketch, "E12.99.0", {"start": v(0.37, 23.8) * mm, "end": v(1.12, 23.79) * mm});
            skCircle(sketch, "E13", {"center": v(0, 0) * mm, "radius": 24.97 * mm});
            skSolve(sketch);
        }
        {
            var Q0;
            Q0 = qSketchRegion(id + "F7", true);
            extrude(context, id + "F8", {"entities" : qUnion([Q0]), "operationType" : NewBodyOperationType.REMOVE, "endBound" : BoundingType.THROUGH_ALL, "oppositeDirection" : true, "depth" : 25.4 * mm});
        }
    });
